# Revit family: Waste_Bin-Sloping_Lid-Servex-Bag_Arms-Rectangular-Magnuson_Group
name_source: partatom
category: Furniture
revit_build: Autodesk Revit 2014 (Build: 20130308_1515(x64)
units: mm (PartAtom-declared; Revit-internal decimal feet)

## types (3) — shared parameters
Color/ Finish = Body in Anodized Silver, Dark Anthracite or Lunar White. Top in Anodized Silver, Dark Anthracite, Lunar White, Capri Blue, Copper Brown, Fern Green or vinyl wrap
Depth = 18.125"
Height = 38.000"
Manufacturer = Magnuson Group
Powder Coat Paint = Dark Anthracite
Type Comments = SLOPE
URL = www.magnusongroup.com
Width = 16.875"

## per-type parameters (varying)
| type | Cost | Description | Lid Type |
| SLP-01 | 595 $ | 38 gallon waste bin with simple top opening, integrated bag arms and non-skid glides | Slope Lid_W : Lid_W |
| SLP-01L-DBL | 915 $ | 38 gallon waste bin with double top opening. Internal rigid liners, integrated bag arms and non-skid glides | Slope Lid_W-P : Lid_W-P |
| SLP-01L | 685 $ | 38 gallon waste bin with simple top opening, internal rigid liner, integrated bag arms and non-skid glides | Slope Lid_W : Lid_W |

note: column(s) folded — value = type name in every type: Model

## geometry (parser evidence)
native form markers: Sweep x5
no freeform markers — native parametric forms only
